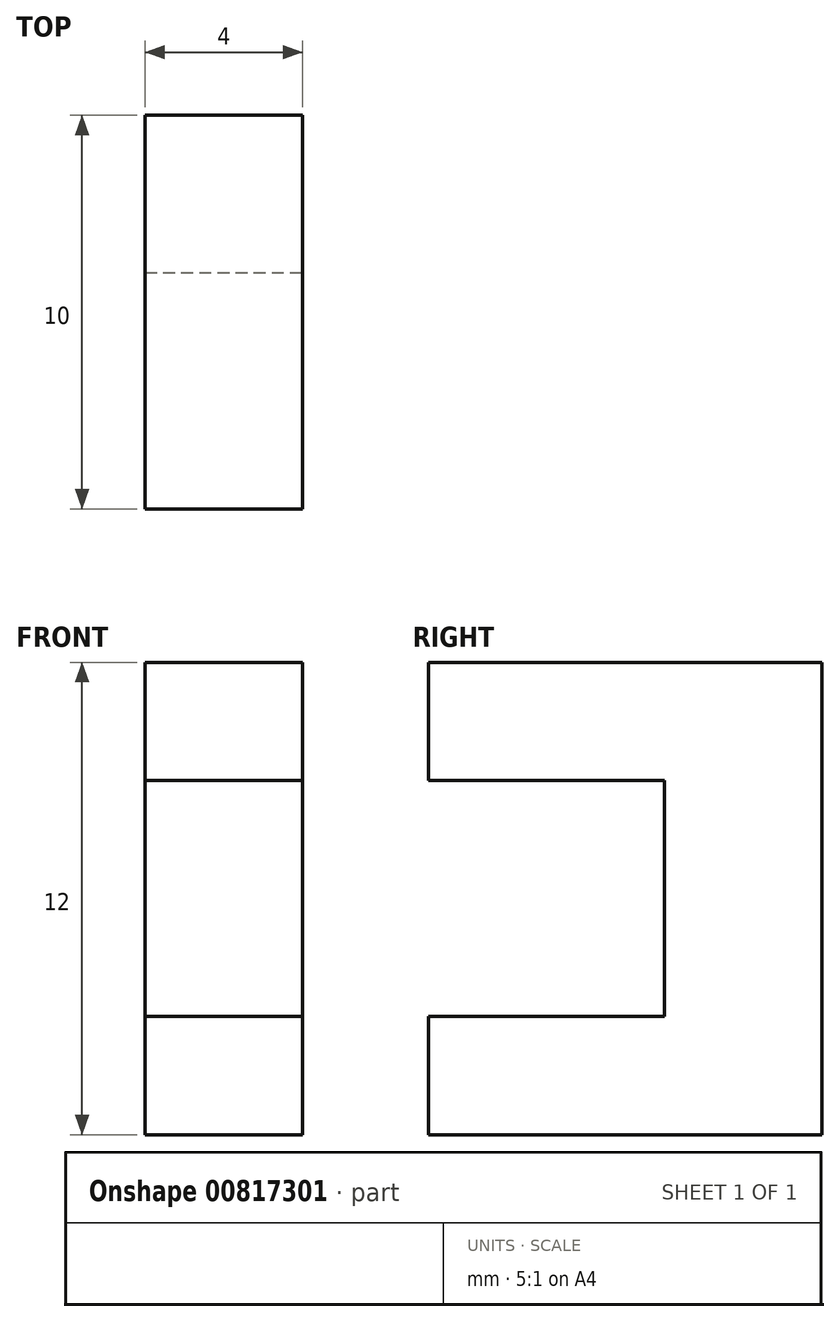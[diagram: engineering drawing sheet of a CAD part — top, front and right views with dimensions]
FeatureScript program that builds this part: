
annotation { "Feature Type Name" : "Feature", "Feature Type Description" : "" }
export const myFeature = defineFeature(function(context is Context, id is Id, definition is map)
    precondition{}
    {
        {
            var Q0;
            Q0=qCreatedBy(makeId("Top.planeOp"),FACE);
            var sketch = newSketch(context, id + "F0", { "sketchPlane" : qUnion([Q0])});
            skLineSegment(sketch, "E0.bottom", {"start": v(2, -5) * mm, "end": v(-2, -5) * mm});
            skLineSegment(sketch, "E0.top", {"start": v(2, 5) * mm, "end": v(-2, 5) * mm});
            skLineSegment(sketch, "E0.left", {"start": v(2, -5) * mm, "end": v(2, 5) * mm});
            skLineSegment(sketch, "E0.right", {"start": v(-2, -5) * mm, "end": v(-2, 5) * mm});
            skPoint(sketch, "E0.middle", {"position": v(0, 0) * mm});
            skLineSegment(sketch, "E1", {"start": v(-2, 5) * mm, "end": v(-2, 1) * mm});
            skLineSegment(sketch, "E2", {"start": v(-2, 1) * mm, "end": v(2, 1) * mm});
            skSolve(sketch);
        }
        {
            var Q0;
            {var subQ0=sQuery(id+"F0.wireOp",EDGE,"E0.top");Q0=makeQuery(id+"F0.imprint","IMPRINT",FACE,{"disambiguationData":[TD([[makeQuery(id+"F0.imprint","IMPRINT",EDGE,{"derivedFrom":subQ0}),1.0]])]});}
            var Q1;
            {var subQ0=sQuery(id+"F0.wireOp",EDGE,"E0.bottom");Q1=makeQuery(id+"F0.imprint","IMPRINT",FACE,{"disambiguationData":[TD([[makeQuery(id+"F0.imprint","IMPRINT",EDGE,{"derivedFrom":subQ0}),-1.0]])]});}
            extrude(context, id + "F1", {"entities" : qUnion([Q0, Q1]), "depth" : 12 * mm, "offsetDistance" : 25 * mm});
        }
        {
            var Q0;
            {var subQ0=sQuery(id+"F0.wireOp",EDGE,"E0.bottom");Q0=makeQuery(id+"F0.imprint","IMPRINT",FACE,{"disambiguationData":[TD([[makeQuery(id+"F0.imprint","IMPRINT",EDGE,{"derivedFrom":subQ0}),-1.0]])]});}
            extrude(context, id + "F2", {"entities" : qUnion([Q0]), "operationType" : NewBodyOperationType.REMOVE, "depth" : 9 * mm, "offsetDistance" : 25 * mm});
        }
        {
            var Q0;
            {var subQ0=sQuery(id+"F0.wireOp",EDGE,"E0.bottom");Q0=makeQuery(id+"F0.imprint","IMPRINT",FACE,{"disambiguationData":[TD([[makeQuery(id+"F0.imprint","IMPRINT",EDGE,{"derivedFrom":subQ0}),-1.0]])]});}
            extrude(context, id + "F3", {"entities" : qUnion([Q0]), "operationType" : NewBodyOperationType.ADD, "depth" : 3 * mm, "offsetDistance" : 25 * mm});
        }
    });
